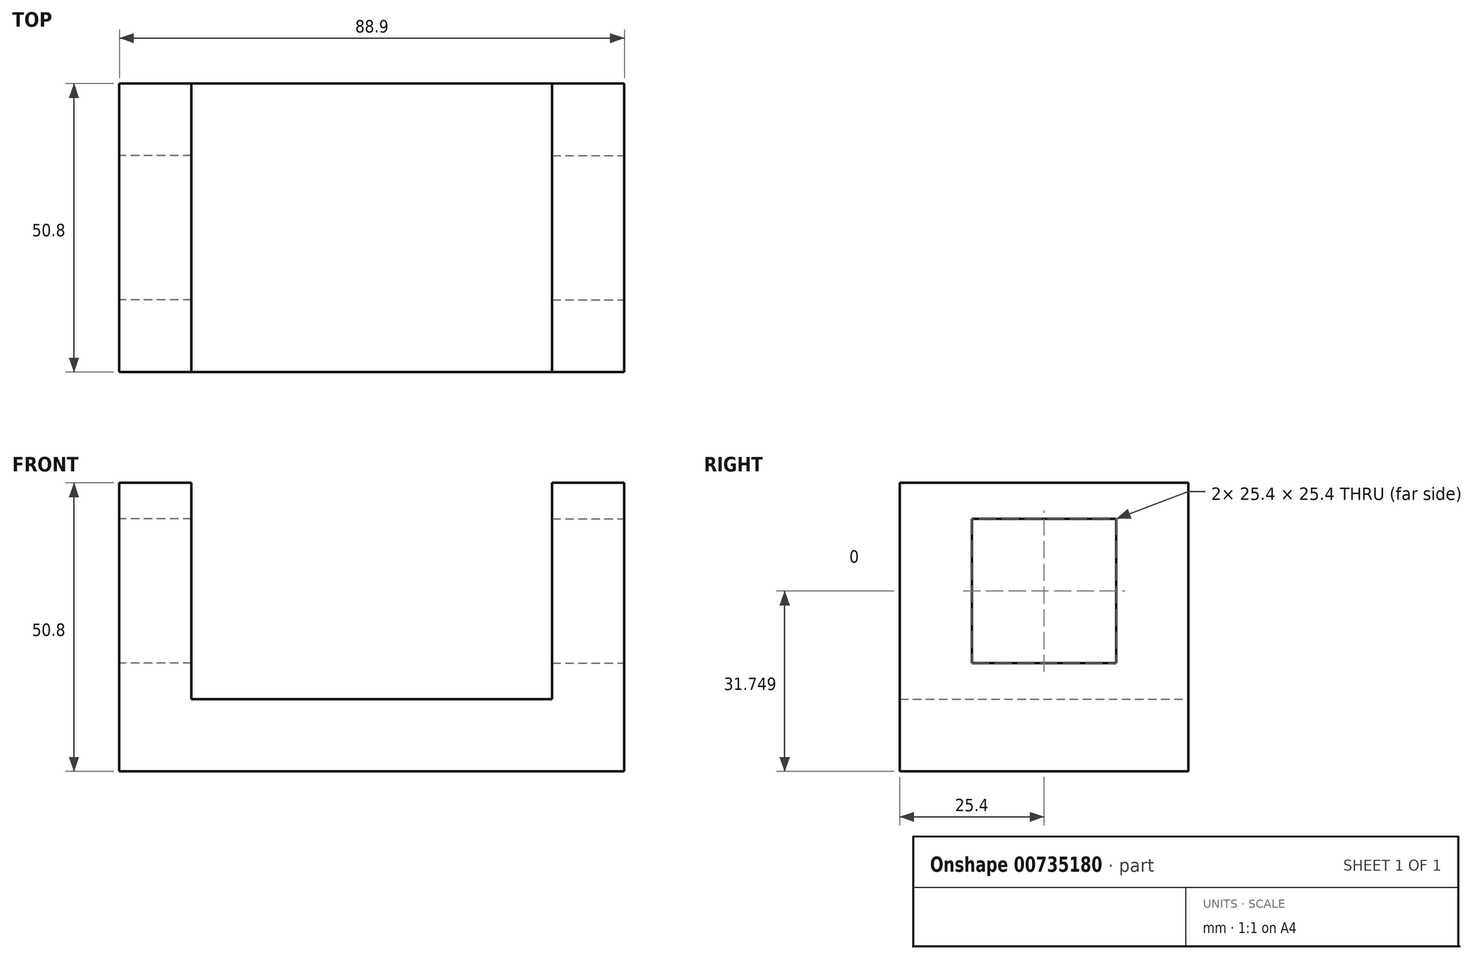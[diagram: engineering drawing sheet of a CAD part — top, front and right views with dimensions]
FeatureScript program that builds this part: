
annotation { "Feature Type Name" : "Feature", "Feature Type Description" : "" }
export const myFeature = defineFeature(function(context is Context, id is Id, definition is map)
    precondition{}
    {
        {
            var Q0;
            Q0=qCreatedBy(makeId("Front.planeOp"),FACE);
            var sketch = newSketch(context, id + "F0", { "sketchPlane" : qUnion([Q0])});
            skLineSegment(sketch, "E0", {"start": v(-47.56, -11.28) * mm, "end": v(41.34, -11.28) * mm});
            skLineSegment(sketch, "E1", {"start": v(-47.56, -11.28) * mm, "end": v(-47.56, 39.52) * mm});
            skLineSegment(sketch, "E2", {"start": v(41.34, -11.28) * mm, "end": v(41.34, 39.52) * mm});
            skLineSegment(sketch, "E3", {"start": v(41.34, 39.52) * mm, "end": v(28.64, 39.52) * mm});
            skLineSegment(sketch, "E4", {"start": v(-47.56, 39.52) * mm, "end": v(-34.86, 39.52) * mm});
            skLineSegment(sketch, "E5", {"start": v(28.64, 39.52) * mm, "end": v(28.64, 1.42) * mm});
            skLineSegment(sketch, "E6", {"start": v(-34.86, 39.52) * mm, "end": v(-34.86, 1.42) * mm});
            skLineSegment(sketch, "E7", {"start": v(-34.86, 1.42) * mm, "end": v(28.64, 1.42) * mm});
            skSolve(sketch);
        }
        {
            var Q0;
            Q0 = qSketchRegion(id + "F0", true);
            extrude(context, id + "F1", {"entities" : qUnion([Q0]), "depth" : 50.8 * mm, "offsetDistance" : 25.4 * mm});
        }
        {
            var Q0;
            Q0=makeQuery(id+"F1.opExtrude","SWEPT_FACE",FACE,{"disambiguationData":[OSD([sQuery(id+"F0.wireOp",EDGE,"E2")])]});
            var sketch = newSketch(context, id + "F2", { "sketchPlane" : qUnion([Q0])});
            skLineSegment(sketch, "E8", {"start": v(-38.1, 33.17) * mm, "end": v(-38.1, 7.77) * mm});
            skLineSegment(sketch, "E9", {"start": v(-38.1, 33.17) * mm, "end": v(-12.7, 33.17) * mm});
            skLineSegment(sketch, "E10", {"start": v(-12.7, 33.17) * mm, "end": v(-12.7, 7.77) * mm});
            skLineSegment(sketch, "E11", {"start": v(-38.1, 7.77) * mm, "end": v(-12.7, 7.77) * mm});
            skLineSegment(sketch, "E12", {"start": v(-38.1, 7.77) * mm, "end": v(-38.1, -11.28) * mm});
            skLineSegment(sketch, "E13", {"start": v(-38.1, -11.28) * mm, "end": v(-50.8, -11.28) * mm});
            skSolve(sketch);
        }
        {
            var Q0;
            Q0=makeQuery(id+"F2.imprint","IMPRINT",FACE,{"disambiguationData":[TD([[makeQuery(id+"F2.imprint","IMPRINT",EDGE,{"derivedFrom":sQuery(id+"F2.wireOp",EDGE,"E8")}),1.0]])]});
            extrude(context, id + "F3", {"entities" : qUnion([Q0]), "operationType" : NewBodyOperationType.REMOVE, "oppositeDirection" : true, "depth" : 12.7 * mm, "offsetDistance" : 25.4 * mm});
        }
        {
            var Q0;
            Q0=makeQuery(id+"F1.opExtrude","SWEPT_FACE",FACE,{"disambiguationData":[OSD([sQuery(id+"F0.wireOp",EDGE,"E1")])]});
            var sketch = newSketch(context, id + "F4", { "sketchPlane" : qUnion([Q0])});
            skLineSegment(sketch, "E14", {"start": v(12.7, 33.17) * mm, "end": v(12.7, 7.77) * mm});
            skLineSegment(sketch, "E15", {"start": v(12.7, 7.77) * mm, "end": v(38.1, 7.77) * mm});
            skLineSegment(sketch, "E16", {"start": v(38.1, 7.77) * mm, "end": v(38.1, 33.17) * mm});
            skLineSegment(sketch, "E17", {"start": v(12.7, 33.17) * mm, "end": v(38.1, 33.17) * mm});
            skSolve(sketch);
        }
        {
            var Q0;
            Q0=makeQuery(id+"F4.imprint","IMPRINT",FACE,{"disambiguationData":[TD([[makeQuery(id+"F4.imprint","IMPRINT",EDGE,{"derivedFrom":sQuery(id+"F4.wireOp",EDGE,"E14")}),1.0]])]});
            extrude(context, id + "F5", {"entities" : qUnion([Q0]), "operationType" : NewBodyOperationType.REMOVE, "endBound" : BoundingType.THROUGH_ALL, "oppositeDirection" : true, "depth" : 12.7 * mm, "offsetDistance" : 25.4 * mm});
        }
    });
